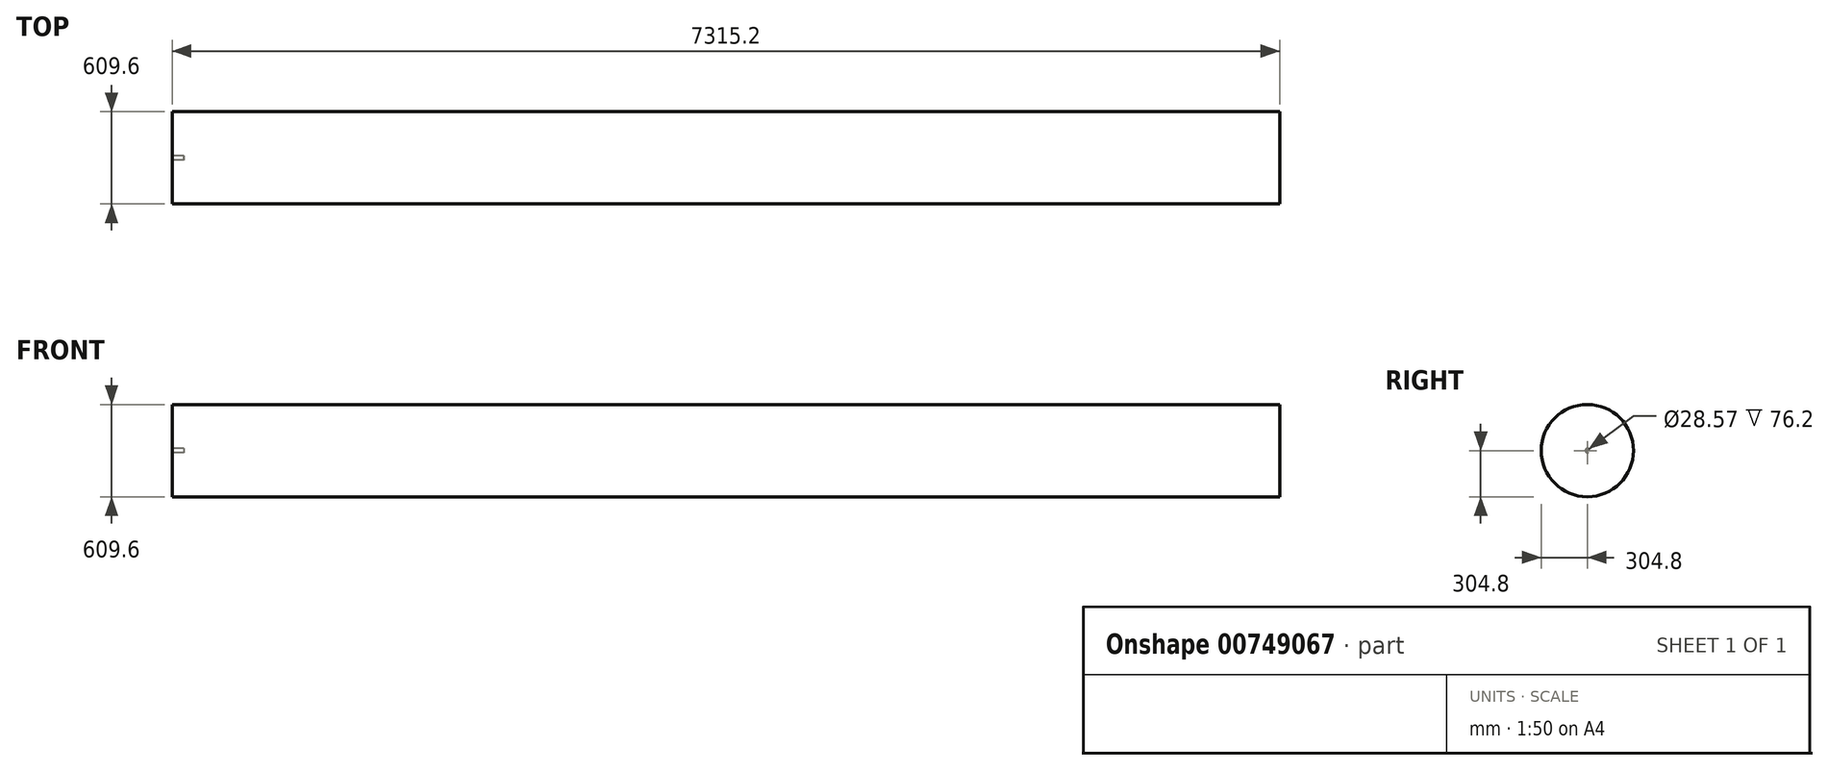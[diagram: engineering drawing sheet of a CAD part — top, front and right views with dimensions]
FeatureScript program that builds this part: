
annotation { "Feature Type Name" : "Feature", "Feature Type Description" : "" }
export const myFeature = defineFeature(function(context is Context, id is Id, definition is map)
    precondition{}
    {
        {
            var Q0;
            Q0=qCreatedBy(makeId("Front.planeOp"),FACE);
            var sketch = newSketch(context, id + "F0", { "sketchPlane" : qUnion([Q0])});
            skLineSegment(sketch, "E0", {"start": v(0, 0) * mm, "end": v(-7315.2, 0) * mm});
            skLineSegment(sketch, "E1", {"start": v(-7315.2, 0) * mm, "end": v(-7315.2, 304.8) * mm});
            skLineSegment(sketch, "E2", {"start": v(-7315.2, 304.8) * mm, "end": v(0, 304.8) * mm});
            skLineSegment(sketch, "E3", {"start": v(0, 304.8) * mm, "end": v(0, 0) * mm});
            skSolve(sketch);
        }
        {
            var Q0;
            Q0 = qSketchRegion(id + "F0", true);
            var Q1;
            Q1=sQuery(id+"F0.wireOp",EDGE,"E0");
            revolve(context, id + "F1", {"surfaceOperationType" : NewSurfaceOperationType.NEW, "entities" : qUnion([Q0]), "axis" : qUnion([Q1]), "revolveType" : RevolveType.FULL});
        }
        {
            var Q0;
            Q0=makeQuery(id+"F1.opRevolve","SWEPT_FACE",FACE,{"disambiguationData":[OSD([sQuery(id+"F0.wireOp",EDGE,"E1")])]});
            var sketch = newSketch(context, id + "F2", { "sketchPlane" : qUnion([Q0])});
            skCircle(sketch, "E4", {"center": v(0, 0) * mm, "radius": 14.29 * mm});
            skSolve(sketch);
        }
        {
            var Q0;
            Q0 = qSketchRegion(id + "F2", true);
            extrude(context, id + "F3", {"entities" : qUnion([Q0]), "operationType" : NewBodyOperationType.REMOVE, "oppositeDirection" : true, "depth" : 76.2 * mm, "offsetDistance" : 25.4 * mm});
        }
    });
